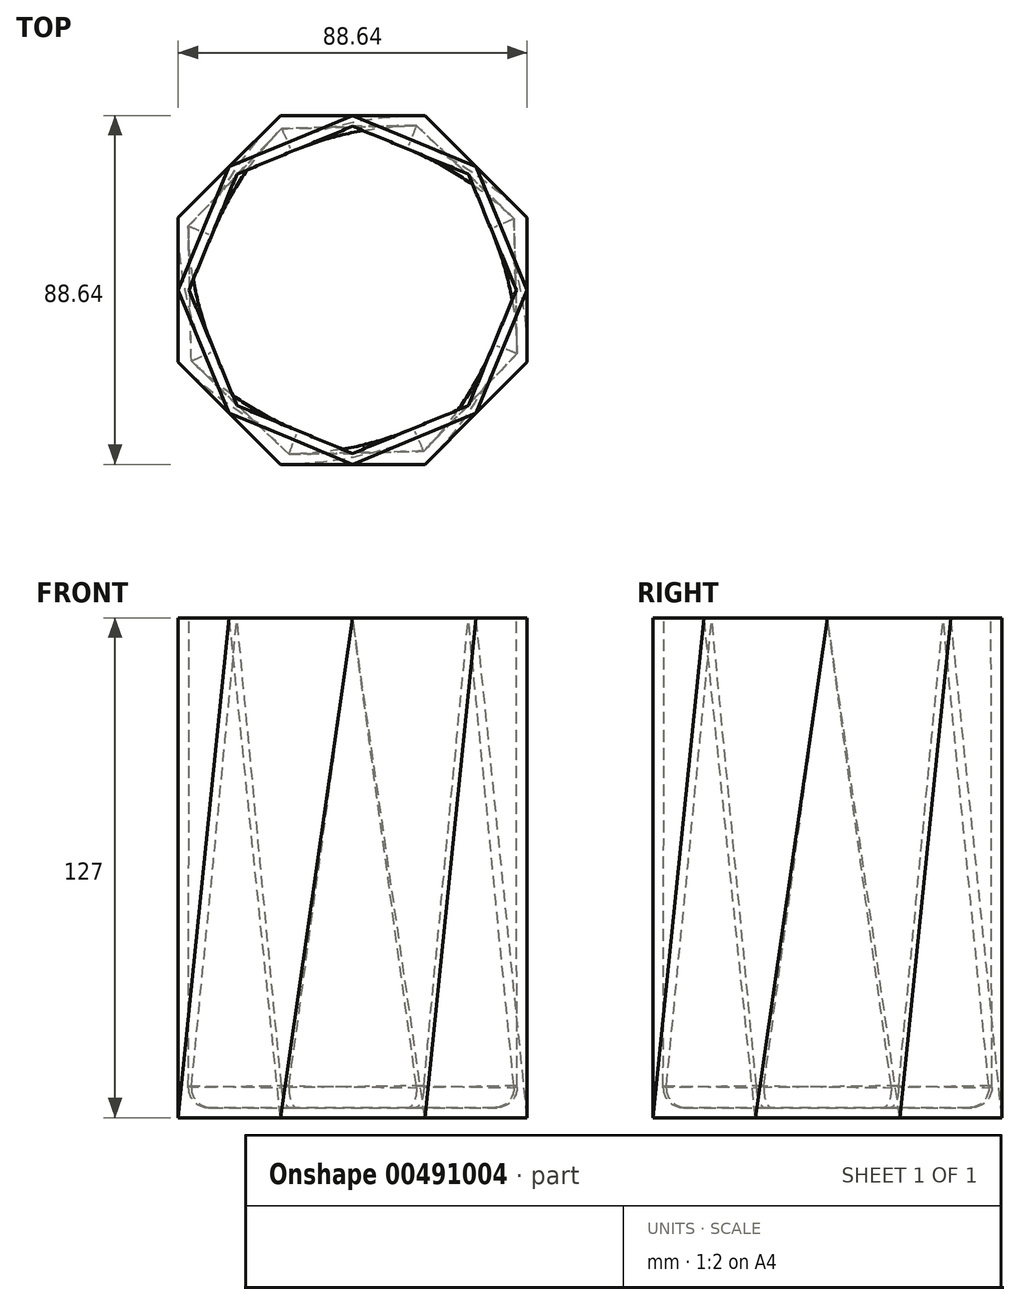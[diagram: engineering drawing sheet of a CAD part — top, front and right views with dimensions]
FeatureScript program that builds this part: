
annotation { "Feature Type Name" : "Feature", "Feature Type Description" : "" }
export const myFeature = defineFeature(function(context is Context, id is Id, definition is map)
    precondition{}
    {
        {
            var Q0;
            Q0=qCreatedBy(makeId("Top.planeOp"),FACE);
            var sketch = newSketch(context, id + "F0", { "sketchPlane" : qUnion([Q0])});
            skCircle(sketch, "E0.cCircle", {"center": v(0, 0) * mm, "radius": 44.32 * mm, "construction": true});
            skLineSegment(sketch, "E0.0", {"start": v(-18.36, 44.32) * mm, "end": v(18.36, 44.32) * mm});
            skLineSegment(sketch, "E0.1", {"start": v(18.36, 44.32) * mm, "end": v(44.32, 18.36) * mm});
            skLineSegment(sketch, "E0.2", {"start": v(44.32, 18.36) * mm, "end": v(44.32, -18.36) * mm});
            skLineSegment(sketch, "E0.3", {"start": v(44.32, -18.36) * mm, "end": v(18.36, -44.32) * mm});
            skLineSegment(sketch, "E0.4", {"start": v(18.36, -44.32) * mm, "end": v(-18.36, -44.32) * mm});
            skLineSegment(sketch, "E0.5", {"start": v(-18.36, -44.32) * mm, "end": v(-44.32, -18.36) * mm});
            skLineSegment(sketch, "E0.6", {"start": v(-44.32, -18.36) * mm, "end": v(-44.32, 18.36) * mm});
            skLineSegment(sketch, "E0.7", {"start": v(-44.32, 18.36) * mm, "end": v(-18.36, 44.32) * mm});
            skPoint(sketch, "E0.0.midPoint", {"position": v(0, 44.32) * mm});
            skSolve(sketch);
        }
        {
            var Q0;
            Q0=qCreatedBy(makeId("Top.planeOp"),FACE);
            cPlane(context, id + "F1", {"entities" : qUnion([Q0]), "cplaneType" : CPlaneType.OFFSET, "offset" : 127 * mm, "width" : 152.4 * mm, "height" : 152.4 * mm});
        }
        {
            var Q0;
            Q0=qCreatedBy(id+"F1.planeOp",FACE);
            var sketch = newSketch(context, id + "F2", { "sketchPlane" : qUnion([Q0])});
            skCircle(sketch, "E1.cCircle", {"center": v(0, 0) * mm, "radius": 40.95 * mm, "construction": true});
            skLineSegment(sketch, "E1.0", {"start": v(44.32, 0) * mm, "end": v(31.34, -31.34) * mm});
            skLineSegment(sketch, "E1.1", {"start": v(31.34, -31.34) * mm, "end": v(0, -44.32) * mm});
            skLineSegment(sketch, "E1.2", {"start": v(0, -44.32) * mm, "end": v(-31.34, -31.34) * mm});
            skLineSegment(sketch, "E1.3", {"start": v(-31.34, -31.34) * mm, "end": v(-44.32, 0) * mm});
            skLineSegment(sketch, "E1.4", {"start": v(-44.32, 0) * mm, "end": v(-31.34, 31.34) * mm});
            skLineSegment(sketch, "E1.5", {"start": v(-31.34, 31.34) * mm, "end": v(0, 44.32) * mm});
            skLineSegment(sketch, "E1.6", {"start": v(0, 44.32) * mm, "end": v(31.34, 31.34) * mm});
            skLineSegment(sketch, "E1.7", {"start": v(31.34, 31.34) * mm, "end": v(44.32, 0) * mm});
            skPoint(sketch, "E1.0.midPoint", {"position": v(37.83, -15.67) * mm});
            skSolve(sketch);
        }
        {
            var Q0;
            Q0=makeQuery(id+"F0.imprint","IMPRINT",FACE,{"disambiguationData":[TD([[makeQuery(id+"F0.imprint","IMPRINT",EDGE,{"derivedFrom":sQuery(id+"F0.wireOp",EDGE,"E0.0")}),-1.0]])]});
            var Q1;
            Q1=makeQuery(id+"F2.imprint","IMPRINT",FACE,{"disambiguationData":[TD([[makeQuery(id+"F2.imprint","IMPRINT",EDGE,{"derivedFrom":sQuery(id+"F2.wireOp",EDGE,"E1.0")}),-1.0]])]});
            loft(context, id + "F3", {"sheetProfilesArray" : [{ "sheetProfileEntities" : qUnion([Q0]) }, { "sheetProfileEntities" : qUnion([Q1]) }]});
        }
        {
            var Q0;
            Q0=makeQuery(id+"F3.opLoft","CAP_FACE",FACE,{"disambiguationData":[OSD([makeQuery(id+"F2.imprint","IMPRINT",FACE,{"disambiguationData":[TD([[makeQuery(id+"F2.imprint","IMPRINT",EDGE,{"derivedFrom":sQuery(id+"F2.wireOp",EDGE,"E1.0")}),-1.0]])]})])],"isStart":true});
            shell(context, id + "F4", {"entities" : qUnion([Q0]), "thickness" : 2.54 * mm});
        }
        {
            var Q0;
            Q0=makeQuery(id+"F4.opShell","OFFSET_FACE",FACE,{"disambiguationData":[OSD([makeQuery(id+"F0.imprint","IMPRINT",FACE,{"disambiguationData":[TD([[makeQuery(id+"F0.imprint","IMPRINT",EDGE,{"derivedFrom":sQuery(id+"F0.wireOp",EDGE,"E0.0")}),-1.0]])]})])]});
            fillet(context, id + "F5", {"entities" : qUnion([Q0]), "radius" : 5.08 * mm, "tangentPropagation" : true, "allowEdgeOverflow" : false});
        }
    });
